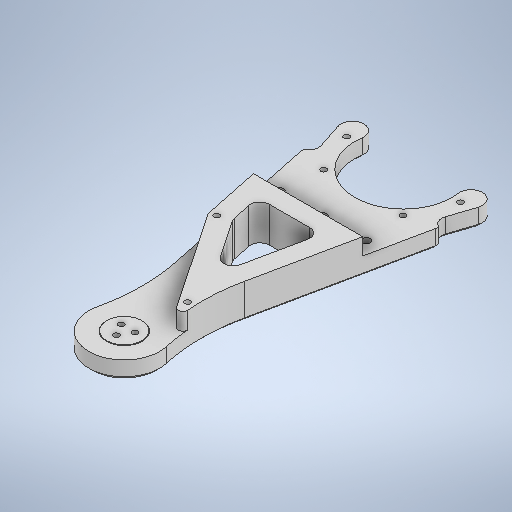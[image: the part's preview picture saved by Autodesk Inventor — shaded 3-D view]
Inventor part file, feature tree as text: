
AUTODESK INVENTOR PART (.ipt)
format: ipt  version: 2025.2 (Build 292293000, 293)  size: 1,284,096 bytes
history: native  units: mm
features: sketch x17, extrude x15, projected_geometry x11, other x7, reference x6, chamfer x2, fillet x2, mirror x1
ambient origin geometry x8: Origin, YZ Plane, XZ Plane, XY Plane, X Axis, Y Axis, Z Axis, Center Point
bodies: Solid1 (feature_tree)
feature tree (61):
  extrude  "Extrusion1"  Depth=52.1mm
  sketch  "Sketch2"  dims[d2=4.0mm d3=6.34888mm]
  extrude  "Extrusion4"  Depth=6.34888mm
  extrude  "Extrusion5"  Depth=80.799962mm
  sketch  "Sketch10"  dims[d8=5.976389mm d9=64.023611mm]
  extrude  "Extrusion8"  Depth=80.799962mm
  extrude  "Extrusion9"  Depth=64.023611mm
  extrude  "Extrusion10"  Depth=35.0mm
  chamfer  "Chamfer1"  Distance=10.137333mm
  extrude  "Extrusion20"  Depth=10.0mm
  extrude  "Extrusion21"  Depth=10.0mm
  extrude  "Extrusion22"  Depth=75.0mm
  extrude  "Extrusion23"  Depth=10.0mm TaperAngle=0.0deg
  extrude  "Extrusion24"  Depth=10.0mm
  fillet  "Fillet2"  Radius=7.05mm
  mirror  "Mirror1"
  extrude  "Extrusion25"  Depth=10.0mm
  extrude  "Extrusion26"  TaperAngle=45.0deg  [1 undecoded]
  extrude  "Extrusion27"  Depth=10.0mm
  fillet  "Fillet3"  Radius=5.6mm
  extrude  "Extrusion28"  Depth=10.0mm
  chamfer  "Chamfer2"  Distance=5.6mm
  sketch  "Sketch1"  dims[d0=3.0mm d1=52.1mm]
  sketch  "Sketch4"  dims[d4=18.882403mm d5=80.799962mm]
  sketch  "Sketch5"  dims[d6=68.556751mm d7=80.799962mm]
  sketch  "Sketch11"  dims[d10=35.0mm d11=35.0mm]
  reference  "Reference11"
  sketch  "Sketch12"  dims[d12=64.023611mm]
  reference  "Reference12"
  reference  "Reference13"
  sketch  "Sketch13"  dims[d13=5.976389mm]
  sketch  "Sketch24"  dims[d14=8.056861mm]
  reference  "Reference20"
  reference  "Reference21"
  projected_geometry  "Projected Loop2"
  sketch  "Sketch25"  dims[d15=48.480908mm]
  reference  "Reference22"
  projected_geometry  "Projected Loop3"
  sketch  "Sketch26"  dims[d16=48.480908mm]
  sketch  "Sketch27"  dims[d17=8.056861mm]
  sketch  "Sketch28"  dims[d18=10.137333mm]
  projected_geometry  "Projected Loop4"
  sketch  "Sketch29"  dims[d19=32.938205mm]
  sketch  "Sketch30"  dims[d20=21.537769mm]
  projected_geometry  "Projected Loop5"
  sketch  "Sketch31"  dims[d21=21.537769mm]
  projected_geometry  "Projected Loop6"
  projected_geometry  "Projected Loop7"
  projected_geometry  "Projected Loop8"
  projected_geometry  "Projected Loop9"
  projected_geometry  "Projected Loop10"
  projected_geometry  "Projected Loop11"
  sketch  "Sketch32"  dims[d22=32.938205mm d23=10.137333mm d24=150.0mm d25=38.0mm d26=75.0mm d28=10.0mm d29=0.0mm d30=48.0mm d31=7.05mm d32=7.05mm d33=45.0deg d40=17.0mm d41=5.6mm d44=5.6mm d45=5.6mm d46=2.8mm d47=2.8mm d48=2.8mm d50=8.5mm d51=3.0mm d52=0.0mm d53=3.0mm d54=3.0mm d55=3.0mm d56=0.0mm d57=0.0mm d63=10.0mm d64=0.0mm d65=0.0mm d66=0.0mm d67=100.0mm d68=10.0mm d69=0.0mm d84=2.0mm d85=2.0mm d86=45.0deg d115=9.0mm d116=0.0mm d117=7.05mm d118=9.0mm d119=0.0mm d120=7.05mm d121=3.0mm d122=3.0mm d123=0.0mm d124=0.0mm d125=5.6mm d126=5.6mm d127=3.0mm d128=0.0mm d129=10.0mm d130=0.0mm d131=0.0mm d132=5.0mm d133=5.6mm d134=5.6mm d135=5.6mm d136=5.6mm d137=3.0mm d138=0.0mm d139=0.2mm d140=0.0mm d141=0.2mm d142=0.0mm d143=0.4mm d144=17.0mm d145=0.85mm d146=0.2mm d147=0.0mm d148=0.2mm d149=2.0mm d150=45.0deg]
  projected_geometry  "Projected Loop12"
  parser-record x2  (decoder bookkeeping rows leaked as tree rows — omitted from the tree; the rows remain in map.json)
  other  "leg_articulation_assembly.iam"
  other  "Big_drum:1"
  other  "WBR.iam"
  other  "leg_wheel:1"
  other  "leg_extend:1"
note: 1 required parameter value undecoded (feature->parameter linkage not recoverable at this tier; creation-order binding heuristic only, values carry confidence <= 0.55)
note: 2 file-system paths scrubbed to <path> (originals preserved in map.json)
